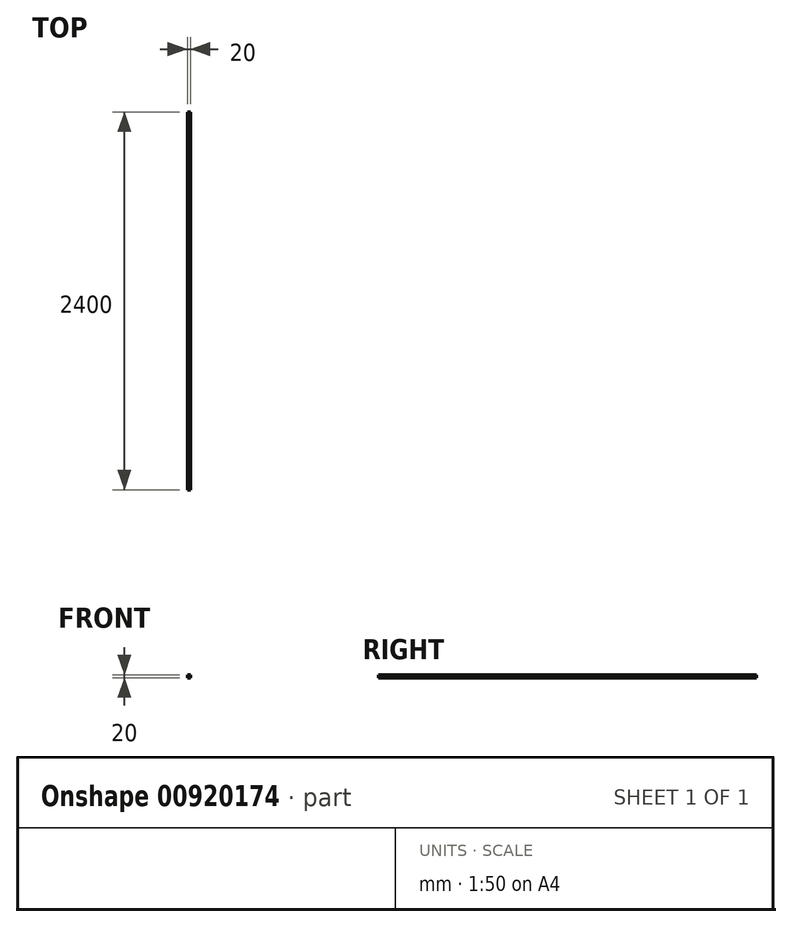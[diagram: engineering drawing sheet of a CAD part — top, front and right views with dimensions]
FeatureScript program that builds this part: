
annotation { "Feature Type Name" : "Feature", "Feature Type Description" : "" }
export const myFeature = defineFeature(function(context is Context, id is Id, definition is map)
    precondition{}
    {
        {
            var Q0;
            Q0=qCreatedBy(makeId("Front.planeOp"),FACE);
            var sketch = newSketch(context, id + "F0", { "sketchPlane" : qUnion([Q0])});
            skLineSegment(sketch, "E0.bottom", {"start": v(-1.9, 12.82) * mm, "end": v(18.1, 12.82) * mm});
            skLineSegment(sketch, "E0.top", {"start": v(-1.9, -7.18) * mm, "end": v(18.1, -7.18) * mm});
            skLineSegment(sketch, "E0.left", {"start": v(-1.9, 12.82) * mm, "end": v(-1.9, -7.18) * mm});
            skLineSegment(sketch, "E0.right", {"start": v(18.1, 12.82) * mm, "end": v(18.1, -7.18) * mm});
            skSolve(sketch);
        }
        {
            var Q0;
            Q0 = qSketchRegion(id + "F0", true);
            extrude(context, id + "F1", {"entities" : qUnion([Q0]), "depth" : 2400 * mm, "offsetDistance" : 25 * mm});
        }
    });
